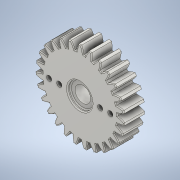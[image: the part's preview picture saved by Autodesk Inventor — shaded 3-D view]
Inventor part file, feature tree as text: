
AUTODESK INVENTOR PART (.ipt)
format: ipt  version: 2022 (Build 260153000, 153)  size: 804,352 bytes
history: native  units: mm (DEFAULTED — no unit token found)
features: sketch x6, extrude x5, plane x3, other x3, fillet x2, pattern_circular x1, projected_geometry x1
ambient origin geometry x8: Origin, YZ Plane, XZ Plane, XY Plane, X Axis, Y Axis, Z Axis, Center Point
bodies: Solid1 (feature_tree)
feature tree (21):
  extrude  "Extrusion1"  Depth=6.0mm TaperAngle=0.0deg
  plane  "Work Plane2"
  plane  "Work Plane8"
  plane  "Work Plane9"
  other  "Цилиндрическое зубчатое зацепление"
  extrude  "Выдавливание5"  Depth=10.0mm TaperAngle=0.0deg
  extrude  "Выдавливание3"  Depth=0.4mm
  extrude  "Выдавливание4"  Depth=0.4mm TaperAngle=0.0deg
  extrude  "Выдавливание6"  TaperAngle=0.0deg  [1 undecoded]
  fillet  "Сопряжение1"  [1 undecoded]
  fillet  "Сопряжение2"  Radius=40.825mm
  pattern_circular  "Круговой массив1"  [2 undecoded]
  sketch  "Sketch1"  dims[d0=43.480844mm d1=6.0mm d2=0.0mm]
  sketch  "Sketch2"  dims[d3=40.5mm d4=10.0mm d5=0.0mm d16=40.825mm d17=0.0mm d34=1.163553mm d39=0.0mm d41=0.0mm d43=40.825mm d46=40.825mm d47=0.0mm d48=0.0mm d52=7.6mm d53=10.0mm d54=2.5mm d55=5.0mm d56=20.0mm d58=360.0deg d60=100.0mm d61=0.0mm d62=5.2mm d67=1.5mm d68=0.0mm d69=5.2mm d70=20.0mm d72=360.0deg d74=4.0mm d75=0.0mm d76=12.0mm d77=1.5mm d78=0.0mm d79=0.5mm d80=0.4mm d81=270.0mm d82=360.0deg]
  other  "Srf1"
  sketch  "Эскиз4"
  sketch  "Эскиз5"
  sketch  "Эскиз6"
  projected_geometry  "Спроецированная петля1"
  sketch  "Эскиз7"
  other  "Средний диаметр"
note: 4 required parameter values undecoded (feature->parameter linkage not recoverable at this tier; creation-order binding heuristic only, values carry confidence <= 0.55)
